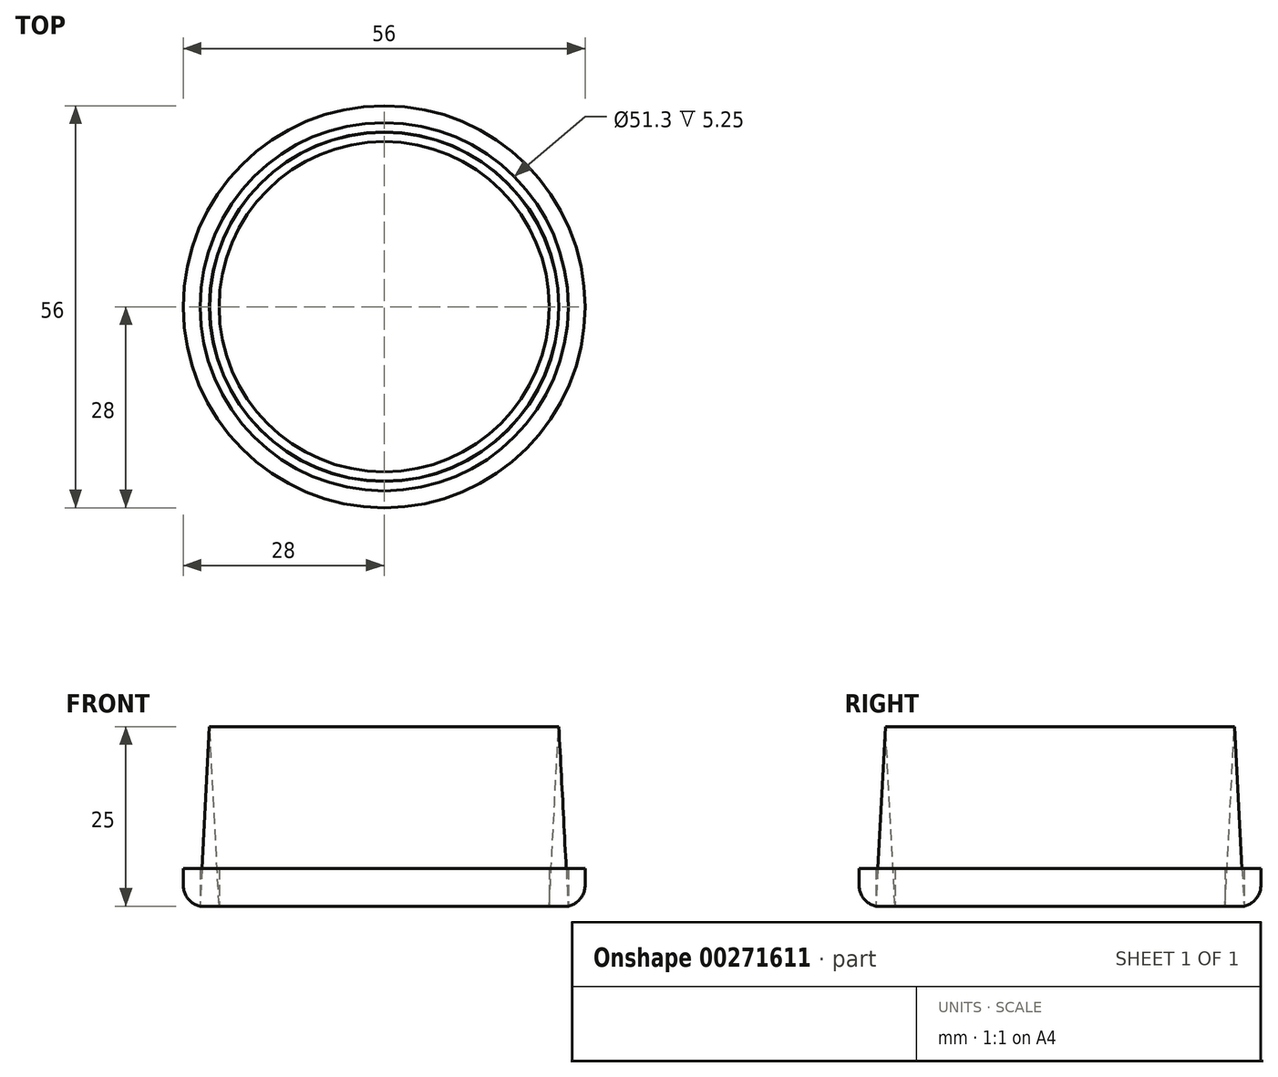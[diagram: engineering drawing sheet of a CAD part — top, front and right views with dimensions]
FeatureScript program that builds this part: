
annotation { "Feature Type Name" : "Feature", "Feature Type Description" : "" }
export const myFeature = defineFeature(function(context is Context, id is Id, definition is map)
    precondition{}
    {
        {
            var Q0;
            Q0=qCreatedBy(makeId("Top.planeOp"),FACE);
            var sketch = newSketch(context, id + "F0", { "sketchPlane" : qUnion([Q0])});
            skCircle(sketch, "E0", {"center": v(0, 0) * mm, "radius": 25.65 * mm});
            skCircle(sketch, "E1.0", {"center": v(0, 0) * mm, "radius": 28 * mm});
            skCircle(sketch, "E2.0", {"center": v(0, 0) * mm, "radius": 23 * mm});
            skSolve(sketch);
        }
        {
            var Q0;
            Q0=makeQuery(id+"F0.imprint","IMPRINT",FACE,{"disambiguationData":[TD([[makeQuery(id+"F0.imprint","IMPRINT",EDGE,{"derivedFrom":sQuery(id+"F0.wireOp",EDGE,"E0")}),1.0]])]});
            extrude(context, id + "F1", {"entities" : qUnion([Q0]), "depth" : 25 * mm, "hasDraft" : true, "draftAngle" : 3 * degree, "draftPullDirection" : true});
        }
        {
            var Q0;
            Q0=makeQuery(id+"F0.imprint","IMPRINT",FACE,{"disambiguationData":[TD([[makeQuery(id+"F0.imprint","IMPRINT",EDGE,{"derivedFrom":sQuery(id+"F0.wireOp",EDGE,"E2.0")}),1.0]])]});
            extrude(context, id + "F2", {"entities" : qUnion([Q0]), "depth" : 5.25 * mm});
        }
        {
            var Q0;
            Q0=makeQuery(id+"F0.imprint","IMPRINT",FACE,{"disambiguationData":[TD([[makeQuery(id+"F0.imprint","IMPRINT",EDGE,{"derivedFrom":sQuery(id+"F0.wireOp",EDGE,"E0")}),-1.0]])]});
            extrude(context, id + "F3", {"entities" : qUnion([Q0]), "depth" : 5.25 * mm});
        }
        {
            var Q0;
            Q0=makeQuery(id+"F3.opExtrude","CAP_EDGE",EDGE,{"disambiguationData":[OSD([sQuery(id+"F0.wireOp",EDGE,"E1.0")])],"isStart":true});
            fillet(context, id + "F4", {"entities" : qUnion([Q0]), "radius" : 3 * mm, "tangentPropagation" : true, "allowEdgeOverflow" : false});
        }
    });
